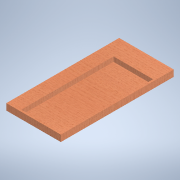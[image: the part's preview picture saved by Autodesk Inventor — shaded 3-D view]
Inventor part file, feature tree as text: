
AUTODESK INVENTOR PART (.ipt)
format: ipt  version: 2022 (Build 260153000, 153)  size: 122,880 bytes
history: native  units: in
note: dims shown in document units (in); Inventor stores cm internally (conversion verified against a paired STEP export)
features: extrude x2, sketch x2
ambient origin geometry x8: Origin, YZ Plane, XZ Plane, XY Plane, X Axis, Y Axis, Z Axis, Center Point
bodies: Solid1 (feature_tree)
feature tree (4):
  extrude  "Extrusion1"  Depth=15.0in
  extrude  "Extrusion2"  Depth=5.25in
  sketch  "Sketch1"  dims[d0=7.25in d1=15.0in]
  sketch  "Sketch2"  dims[d2=0.852in d3=0.0in d4=5.25in d5=12.75in d6=0.0in d7=0.0in d8=0.709in d9=0.0in]
